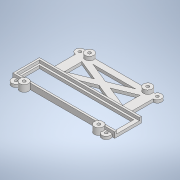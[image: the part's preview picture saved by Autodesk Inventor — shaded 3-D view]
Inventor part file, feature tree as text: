
AUTODESK INVENTOR PART (.ipt)
format: ipt  version: 2020.4 (Build 244396000, 396)  size: 241,152 bytes
history: native  units: mm
features: reference x19, other x9, extrude x3, sketch x3
ambient origin geometry x8: Origin, YZ Plane, XZ Plane, XY Plane, X Axis, Y Axis, Z Axis, Center Point
bodies: Solid1 (feature_tree)
feature tree (34):
  extrude  "Extrusion1"  Depth=2.0mm
  extrude  "Extrusion2"  Depth=3.0mm
  extrude  "Extrusion3"  Depth=3.0mm
  sketch  "Sketch1"  dims[d0=2.0mm d1=2.0mm]
  reference  "Reference1"
  reference  "Reference2"
  reference  "Reference3"
  reference  "Reference4"
  reference  "Reference5"
  reference  "Reference6"
  reference  "Reference7"
  reference  "Reference8"
  reference  "Reference9"
  sketch  "Sketch2"  dims[d2=3.0mm d3=3.0mm]
  reference  "Reference10"
  reference  "Reference11"
  reference  "Reference12"
  reference  "Reference13"
  sketch  "Sketch3"  dims[d4=3.0mm d5=3.0mm d6=3.0mm d7=3.0mm d8=3.0mm d9=3.0mm d10=6.199922mm d11=6.199922mm d12=6.199922mm d13=3.099961mm d14=3.099961mm d15=3.0mm d16=0.0mm d18=3.0mm d19=0.0mm d20=4.0mm d21=0.0mm]
  reference  "Reference14"
  reference  "Reference15"
  reference  "Reference16"
  reference  "Reference17"
  reference  "Reference18"
  reference  "Reference19"
  other  "<userpath>\Dokumentumok\BME\Dipterv\3d\robot_v2_turnigy.iam"
  other  "robot_v2_turnigy.iam"
  other  "turnigy_battery:1"
  other  "electronics:1"
  other  "main_board:1"
  other  "PCB Component:1"
  other  "Board:1"
  other  "bottom2_turnigy:1"
  other  "tavtarto_30mm:4"
